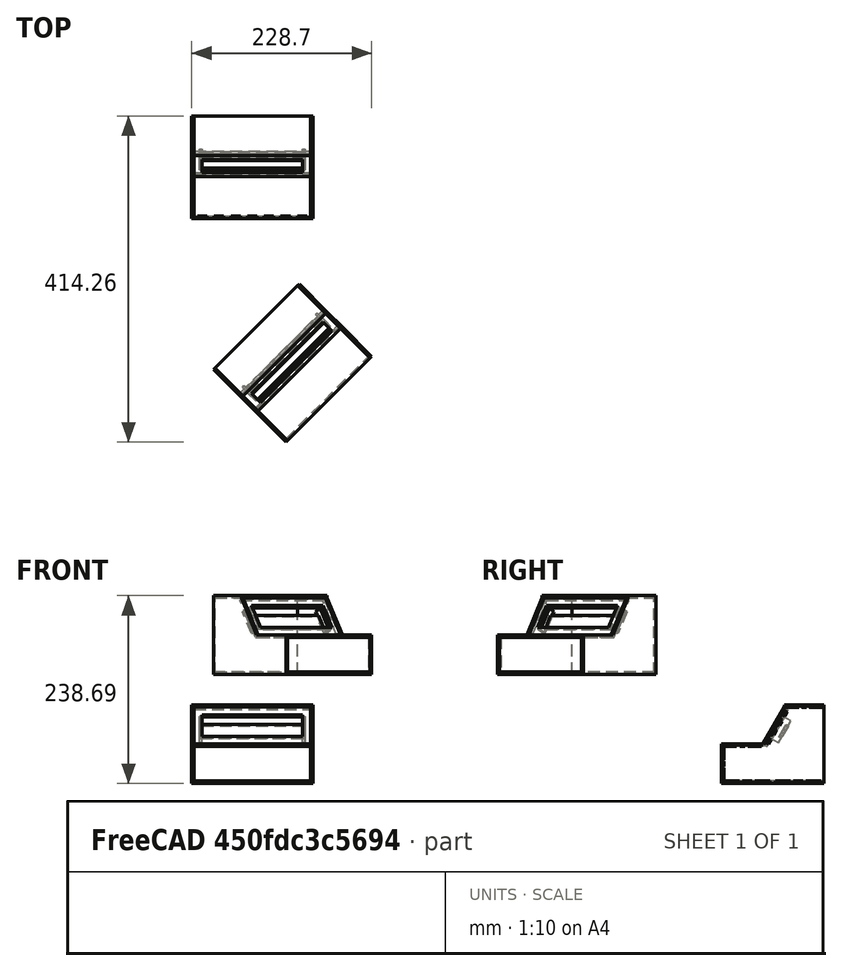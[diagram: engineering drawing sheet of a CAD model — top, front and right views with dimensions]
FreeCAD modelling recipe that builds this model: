
FCSTD DOCUMENT  (FreeCAD 0.21R33668 +26 (Git))
Label: support_4_matrix
License: All rights reserved
LicenseURL: https://en.wikipedia.org/wiki/All_rights_reserved
objects: Part::Feature×36, Sketcher::SketchObject×18, PartDesign::Pad×11, PartDesign::Body×11, Part::Part2DObjectPython×11, PartDesign::Pocket×7, App::DocumentObjectGroup×7, Part::FeaturePython×5, App::FeaturePython×4, Spreadsheet::Sheet×1, PartDesign::Plane×1, App::Part×1
note: 118 computed .brp shape members not serialized (recipe doc carries the construction recipe); baked Part::Feature solids carry a one-line shape summary decoded from their .brp

FEATURE [Sketcher::SketchObject] Sketch
  FullyConstrained = true
  MapMode = 5
  Placement = pos=(0,0,0) rot=(1,0,0;1.5708rad)
  Support = -> [XZ_Plane]
  expr: Constraints[10] = <<dimensions>>.lg_plaque
  expr: Constraints[9] = <<dimensions>>.ep_plaque
  sketch-geometry (4):
    g0: LineSegment StartX=0 StartY=0 StartZ=0 EndX=148 EndY=0 EndZ=0
    g1: LineSegment StartX=148 StartY=0 StartZ=0 EndX=148 EndY=3 EndZ=0
    g2: LineSegment StartX=148 StartY=3 StartZ=0 EndX=0 EndY=3 EndZ=0
    g3: LineSegment StartX=0 StartY=3 StartZ=0 EndX=0 EndY=0 EndZ=0
  constraints (11):
    c: Coincident(g0,g1)
    c: Coincident(g1,g2)
    c: Coincident(g2,g3)
    c: Coincident(g3,g0)
    c: Horizontal(g0)
    c: Horizontal(g2)
    c: Vertical(g1)
    c: Vertical(g3)
    c: Coincident(g0,g-1)
    c: DistanceY(g3,g3) = 3
    c: DistanceX(g2,g2) = 148
FEATURE [Spreadsheet::Sheet] Spreadsheet  label="dimensions"
  cells = A1='ep_plaque; B1='lrg_plaque; C1='lg_plaque; E1='ht_plaque; A2(ep_plaque)==3 mm; B2(lrg_plaque)==130 mm; C2(lg_plaque)==4 * lrg_matrix + 2 * dist_lateral_matrix; D2='4*32+2*2; E2(ht_plaque)==100 mm; F2='32+50+2; E3='ht_plat; A4='angle_display; B4='dist_top; E4(ht_plat)==50 mm; A5(angle_display)==120 °; B5(dist_top)==50 mm; E5='ht_display; E6==lg_display * cos(180 ° - (180 ° - angle_display) - 90 °); A7='lg_display; B7='dist_display; C7='lg_display = hypotenus; F7='Sin/cos -> degres by default; A8(lg_display)==(ht_plaque - ht_plat - ep_plaque) / sin(180 ° - angle_display); B8(dist_display)==(ht_plaque - ht_plat - ep_plaque) * cos(180 ° - angle_display) / sin(180 ° - angle_display); B10='dist_plat; B11(dist_plat)==lrg_plaque - dist_top - dist_display; A13='lrg_matrix; B13='dist_lateral_matrix; D13='ep_supp_ar; A14(lrg_matrix)==32 mm; B14(dist_lateral_matrix)==10 mm; D14(ep_supp_ar)==7 mm + ep_plaque; E14='Epaisseur; D15='ep_protu_supp_arr; D16(ep_protu_supp_ar)==10 mm; E16='Epaisseur protusion; A17='Informations; B17='Limitation /!\; D17='lg_side_supp; A18='Le trou de l'afficheur est centré; D18(lg_side_supp)==8 mm; D19='dph_supp; D20(dph_supp)==7 mm; D21='lrg_supp_ar; D22(lrg_supp_ar)==18 mm
FEATURE [PartDesign::Pad] Pad
  Direction = (0,-1,-2e-16)
  Length = 130
  Length2 = 10
  Placement = pos=(0,0,0) rot=(1,0,0;1.5708rad)
  Profile = -> Sketch
  ReferenceAxis = -> Sketch [N_Axis]
  Type = 0
  expr: Length = <<dimensions>>.lrg_plaque
FEATURE [PartDesign::Body] Body  label="plaque_dessous"
  Group = -> [Sketch,Pad]
  Origin = -> Origin
  Tip = -> Pad
FEATURE [Sketcher::SketchObject] Sketch001
  FullyConstrained = true
  MapMode = 5
  Support = -> [XY_Plane001]
  expr: Constraints[10] = <<dimensions>>.lrg_plaque
  expr: Constraints[9] = <<dimensions>>.ep_plaque
  sketch-geometry (4):
    g0: LineSegment StartX=-3 StartY=-130 StartZ=0 EndX=0 EndY=-130 EndZ=0
    g1: LineSegment StartX=0 StartY=-130 StartZ=0 EndX=0 EndY=0 EndZ=0
    g2: LineSegment StartX=0 StartY=0 StartZ=0 EndX=-3 EndY=0 EndZ=0
    g3: LineSegment StartX=-3 StartY=0 StartZ=0 EndX=-3 EndY=-130 EndZ=0
  constraints (11):
    c: Coincident(g0,g1)
    c: Coincident(g1,g2)
    c: Coincident(g2,g3)
    c: Coincident(g3,g0)
    c: Horizontal(g0)
    c: Horizontal(g2)
    c: Vertical(g1)
    c: Vertical(g3)
    c: Coincident(g1,g-1)
    c: DistanceX(g2,g2) = 3
    c: DistanceY(g3,g3) = 130
FEATURE [PartDesign::Pad] Pad001
  Direction = (0,0,1)
  Length = 100
  Length2 = 10
  Profile = -> Sketch001
  ReferenceAxis = -> Sketch001 [N_Axis]
  Type = 0
  expr: Length = <<dimensions>>.ht_plaque
FEATURE [Sketcher::SketchObject] Sketch002
  ExternalGeometry = -> [Pad001]
  FullyConstrained = true
  MapMode = 5
  Placement = pos=(-3,0,0) rot=(0.57735,-0.57735,-0.57735;2.0944rad)
  Support = -> [Pad001]
  expr: Constraints[11] = <<dimensions>>.angle_display
  expr: Constraints[12] = <<dimensions>>.dist_top
  expr: Constraints[13] = <<dimensions>>.ht_plaque - <<dimensions>>.ep_plaque
  expr: Constraints[6] = <<dimensions>>.ht_plat
  sketch-geometry (5):
    g0: LineSegment StartX=50 StartY=100 StartZ=0 EndX=130 EndY=100 EndZ=0
    g1: LineSegment StartX=130 StartY=100 StartZ=0 EndX=130 EndY=50 EndZ=0
    g2: LineSegment StartX=130 StartY=50 StartZ=0 EndX=77.1355 EndY=50 EndZ=0
    g3: LineSegment StartX=50 StartY=100 StartZ=0 EndX=50 EndY=97 EndZ=0
    g4: LineSegment StartX=50 StartY=97 StartZ=0 EndX=77.1355 EndY=50 EndZ=0
  constraints (14):
    c: Horizontal(g0)
    c: Coincident(g0,g1)
    c: Coincident(g1,g2)
    c: Horizontal(g2)
    c: Coincident(g0,g-4)
    c: PointOnObject(g1,g-4)
    c: DistanceY(g-4,g1) = 50
    c: Coincident(g0,g3)
    c: Vertical(g3)
    c: Coincident(g3,g4)
    c: Coincident(g4,g2)
    c: Angle(g2,g4) = 2.0944
    c: DistanceX(g-1,g3) = 50
    c: DistanceY(g-1,g3) = 97
FEATURE [PartDesign::Pocket] Pocket
  BaseFeature = -> Pad001
  Direction = (1,0,0)
  Length = 5
  Length2 = 5
  Profile = -> Sketch002
  ReferenceAxis = -> Sketch002 [N_Axis]
  Type = 1
FEATURE [PartDesign::Body] Body001  label="plaque_gauche"
  Group = -> [Sketch001,Pad001,Sketch002,Pocket]
  Origin = -> Origin001
  Tip = -> Pocket
FEATURE [Sketcher::SketchObject] Sketch003
  FullyConstrained = true
  MapMode = 5
  Support = -> [XY_Plane002]
  expr: Constraints[10] = <<dimensions>>.lg_plaque
  expr: Constraints[11] = <<dimensions>>.lrg_plaque
  expr: Constraints[9] = <<dimensions>>.ep_plaque
  sketch-geometry (4):
    g0: LineSegment StartX=148 StartY=0 StartZ=0 EndX=151 EndY=0 EndZ=0
    g1: LineSegment StartX=151 StartY=0 StartZ=0 EndX=151 EndY=-130 EndZ=0
    g2: LineSegment StartX=151 StartY=-130 StartZ=0 EndX=148 EndY=-130 EndZ=0
    g3: LineSegment StartX=148 StartY=-130 StartZ=0 EndX=148 EndY=0 EndZ=0
  constraints (12):
    c: Coincident(g0,g1)
    c: Coincident(g1,g2)
    c: Coincident(g2,g3)
    c: Coincident(g3,g0)
    c: Horizontal(g0)
    c: Horizontal(g2)
    c: Vertical(g1)
    c: Vertical(g3)
    c: PointOnObject(g0,g-1)
    c: DistanceX(g0,g0) = 3
    c: DistanceX(g-1,g0) = 148
    c: DistanceY(g1,g1) = 130
FEATURE [PartDesign::Pad] Pad002
  Direction = (0,0,1)
  Length = 100
  Length2 = 10
  Profile = -> Sketch003
  ReferenceAxis = -> Sketch003 [N_Axis]
  Type = 0
  expr: Length = <<dimensions>>.ht_plaque
FEATURE [Sketcher::SketchObject] Sketch004
  ExternalGeometry = -> [Pad002]
  FullyConstrained = true
  MapMode = 5
  Placement = pos=(151,0,0) rot=(0.57735,0.57735,0.57735;2.0944rad)
  Support = -> [Pad002]
  expr: Constraints[10] = <<dimensions>>.ht_plaque - <<dimensions>>.ep_plaque
  expr: Constraints[13] = <<dimensions>>.dist_top
  expr: Constraints[6] = <<dimensions>>.angle_display
  expr: Constraints[7] = <<dimensions>>.ht_plat
  sketch-geometry (5):
    g0: LineSegment StartX=-130 StartY=50 StartZ=0 EndX=-77.1355 EndY=50 EndZ=0
    g1: LineSegment StartX=-50 StartY=100 StartZ=0 EndX=-130 EndY=100 EndZ=0
    g2: LineSegment StartX=-130 StartY=100 StartZ=0 EndX=-130 EndY=50 EndZ=0
    g3: LineSegment StartX=-50 StartY=100 StartZ=0 EndX=-50 EndY=97 EndZ=0
    g4: LineSegment StartX=-50 StartY=97 StartZ=0 EndX=-77.1355 EndY=50 EndZ=0
  constraints (14):
    c: Coincident(g1,g2)
    c: Coincident(g2,g0)
    c: Coincident(g1,g-4)
    c: Coincident(g1,g3)
    c: Coincident(g3,g4)
    c: Coincident(g4,g0)
    c: Angle(g4,g0) = 2.0944
    c: DistanceY(g-4,g0) = 50
    c: Perpendicular(g0,g2)
    c: PointOnObject(g0,g-4)
    c: DistanceY(g-4,g3) = 97
    c: PointOnObject(g1,g-3)
    c: Perpendicular(g3,g1)
    c: DistanceX(g1,g-3) = 50
FEATURE [PartDesign::Pocket] Pocket001
  BaseFeature = -> Pad002
  Direction = (-1,0,0)
  Length = 5
  Length2 = 5
  Profile = -> Sketch004
  ReferenceAxis = -> Sketch004 [N_Axis]
  Type = 1
FEATURE [PartDesign::Body] Body002  label="plaque_droite"
  Group = -> [Sketch003,Pad002,Sketch004,Pocket001]
  Origin = -> Origin002
  Tip = -> Pocket001
FEATURE [Sketcher::SketchObject] Sketch005
  FullyConstrained = true
  MapMode = 5
  Placement = pos=(0,0,0) rot=(0.57735,0.57735,0.57735;2.0944rad)
  Support = -> [YZ_Plane003]
  expr: Constraints[10] = <<dimensions>>.ht_plaque
  expr: Constraints[11] = <<dimensions>>.ep_plaque
  expr: Constraints[9] = <<dimensions>>.dist_top
  sketch-geometry (4):
    g0: LineSegment StartX=-50 StartY=97 StartZ=0 EndX=0 EndY=97 EndZ=0
    g1: LineSegment StartX=0 StartY=97 StartZ=0 EndX=0 EndY=100 EndZ=0
    g2: LineSegment StartX=0 StartY=100 StartZ=0 EndX=-50 EndY=100 EndZ=0
    g3: LineSegment StartX=-50 StartY=100 StartZ=0 EndX=-50 EndY=97 EndZ=0
  constraints (12):
    c: Coincident(g0,g1)
    c: Coincident(g1,g2)
    c: Coincident(g2,g3)
    c: Coincident(g3,g0)
    c: Horizontal(g0)
    c: Horizontal(g2)
    c: Vertical(g1)
    c: Vertical(g3)
    c: PointOnObject(g0,g-2)
    c: DistanceX(g0,g0) = 50
    c: DistanceY(g-1,g1) = 100
    c: DistanceY(g1,g1) = 3
FEATURE [PartDesign::Pad] Pad003
  Direction = (1,-2e-16,3e-16)
  Length = 148
  Length2 = 10
  Placement = pos=(0,0,0) rot=(0.57735,0.57735,0.57735;2.0944rad)
  Profile = -> Sketch005
  ReferenceAxis = -> Sketch005 [N_Axis]
  Type = 0
  expr: Length = <<dimensions>>.lg_plaque
FEATURE [PartDesign::Body] Body003  label="plaque_dessus_haut"
  Group = -> [Sketch005,Pad003]
  Origin = -> Origin003
  Tip = -> Pad003
FEATURE [Sketcher::SketchObject] Sketch006
  FullyConstrained = true
  MapMode = 5
  Placement = pos=(0,0,0) rot=(0.57735,0.57735,0.57735;2.0944rad)
  Support = -> [YZ_Plane004]
  expr: Constraints[10] = <<dimensions>>.ht_plat - <<dimensions>>.ep_plaque * cos(180 ° - <<dimensions>>.angle_display)
  expr: Constraints[11] = <<dimensions>>.ht_plaque - <<dimensions>>.ep_plaque * sin(<<dimensions>>.angle_display - 90 °) - <<dimensions>>.ep_plaque
  expr: Constraints[4] = <<dimensions>>.ht_plat
  expr: Constraints[5] = <<dimensions>>.dist_top + <<dimensions>>.dist_display
  expr: Constraints[6] = <<dimensions>>.ht_plaque - <<dimensions>>.ep_plaque
  expr: Constraints[7] = <<dimensions>>.dist_top
  sketch-geometry (4):
    g0: LineSegment StartX=-74.5374 StartY=48.5 StartZ=0 EndX=-47.4019 EndY=95.5 EndZ=0
    g1: LineSegment StartX=-47.4019 StartY=95.5 StartZ=0 EndX=-50 EndY=97 EndZ=0
    g2: LineSegment StartX=-50 StartY=97 StartZ=0 EndX=-77.1355 EndY=50 EndZ=0
    g3: LineSegment StartX=-77.1355 StartY=50 StartZ=0 EndX=-74.5374 EndY=48.5 EndZ=0
  constraints (12):
    c: Coincident(g0,g1)
    c: Coincident(g1,g2)
    c: Coincident(g2,g3)
    c: Coincident(g3,g0)
    c: DistanceY(g-1,g2) = 50
    c: DistanceX(g2,g-1) = 77.1355
    c: DistanceY(g-1,g1) = 97
    c: DistanceX(g1,g-1) = 50
    c: Perpendicular(g3,g2)
    c: Perpendicular(g2,g1)
    c: DistanceY(g-1,g0) = 48.5
    c: DistanceY(g-1,g0) = 95.5
FEATURE [Sketcher::SketchObject] Sketch008
  FullyConstrained = true
  MapMode = 5
  Placement = pos=(0,0,0) rot=(0.57735,0.57735,0.57735;2.0944rad)
  Support = -> [YZ_Plane005]
  expr: Constraints[10] = <<dimensions>>.lrg_plaque
  expr: Constraints[11] = <<dimensions>>.ht_plat
  expr: Constraints[8] = <<dimensions>>.ep_plaque
  expr: Constraints[9] = <<dimensions>>.dist_plat
  sketch-geometry (4):
    g0: LineSegment StartX=-130 StartY=50 StartZ=0 EndX=-77.1355 EndY=50 EndZ=0
    g1: LineSegment StartX=-77.1355 StartY=50 StartZ=0 EndX=-77.1355 EndY=47 EndZ=0
    g2: LineSegment StartX=-77.1355 StartY=47 StartZ=0 EndX=-130 EndY=47 EndZ=0
    g3: LineSegment StartX=-130 StartY=47 StartZ=0 EndX=-130 EndY=50 EndZ=0
  constraints (12):
    c: Coincident(g0,g1)
    c: Coincident(g1,g2)
    c: Coincident(g2,g3)
    c: Coincident(g3,g0)
    c: Horizontal(g0)
    c: Horizontal(g2)
    c: Vertical(g1)
    c: Vertical(g3)
    c: DistanceY(g3,g3) = 3
    c: DistanceX(g0,g0) = 52.8645
    c: DistanceX(g0,g-1) = 130
    c: DistanceY(g-1,g0) = 50
FEATURE [PartDesign::Pad] Pad005
  Direction = (1,-2e-16,3e-16)
  Length = 148
  Length2 = 10
  Placement = pos=(0,0,0) rot=(0.57735,0.57735,0.57735;2.0944rad)
  Profile = -> Sketch008
  ReferenceAxis = -> Sketch008 [N_Axis]
  Type = 0
  expr: Length = <<dimensions>>.lg_plaque
FEATURE [PartDesign::Body] Body005  label="plaque_plat"
  Group = -> [Sketch008,Pad005]
  Origin = -> Origin005
  Tip = -> Pad005
FEATURE [Sketcher::SketchObject] Sketch009
  FullyConstrained = true
  MapMode = 5
  Placement = pos=(0,0,0) rot=(0.57735,0.57735,0.57735;2.0944rad)
  Support = -> [YZ_Plane006]
  expr: Constraints[10] = <<dimensions>>.lrg_plaque
  expr: Constraints[11] = <<dimensions>>.ht_plat - 2 * <<dimensions>>.ep_plaque
  expr: Constraints[8] = <<dimensions>>.ep_plaque
  expr: Constraints[9] = <<dimensions>>.ht_plat - <<dimensions>>.ep_plaque
  sketch-geometry (4):
    g0: LineSegment StartX=-130 StartY=47 StartZ=0 EndX=-127 EndY=47 EndZ=0
    g1: LineSegment StartX=-127 StartY=47 StartZ=0 EndX=-127 EndY=3 EndZ=0
    g2: LineSegment StartX=-127 StartY=3 StartZ=0 EndX=-130 EndY=3 EndZ=0
    g3: LineSegment StartX=-130 StartY=3 StartZ=0 EndX=-130 EndY=47 EndZ=0
  constraints (12):
    c: Coincident(g0,g1)
    c: Coincident(g1,g2)
    c: Coincident(g2,g3)
    c: Coincident(g3,g0)
    c: Horizontal(g0)
    c: Horizontal(g2)
    c: Vertical(g1)
    c: Vertical(g3)
    c: DistanceX(g0,g0) = 3
    c: DistanceY(g-1,g0) = 47
    c: DistanceX(g0,g-1) = 130
    c: DistanceY(g1,g1) = 44
FEATURE [PartDesign::Pad] Pad006
  Direction = (1,-2e-16,3e-16)
  Length = 148
  Length2 = 10
  Placement = pos=(0,0,0) rot=(0.57735,0.57735,0.57735;2.0944rad)
  Profile = -> Sketch009
  ReferenceAxis = -> Sketch009 [N_Axis]
  Type = 0
  expr: Length = <<dimensions>>.lg_plaque
FEATURE [PartDesign::Body] Body006  label="plaque_avant"
  Group = -> [Sketch009,Pad006]
  Origin = -> Origin006
  Tip = -> Pad006
FEATURE [PartDesign::Pad] Pad007
  Direction = (1,-2e-16,3e-16)
  Length = 148
  Length2 = 10
  Placement = pos=(0,0,0) rot=(0.57735,0.57735,0.57735;2.0944rad)
  Profile = -> Sketch006
  ReferenceAxis = -> Sketch006 [N_Axis]
  Type = 0
  expr: Length = <<dimensions>>.lg_plaque
FEATURE [Sketcher::SketchObject] Sketch010
  ExternalGeometry = -> [Pad007]
  FullyConstrained = true
  MapMode = 5
  Placement = pos=(-4.77e-14,-79.5022,45.9006) rot=(0.447214,0.447214,-0.774597;1.82348rad)
  Support = -> [Pad007]
  expr: Constraints[10] = (<<dimensions>>.lg_plaque - 4 * <<dimensions>>.lrg_matrix) / 2
  expr: Constraints[11] = (<<dimensions>>.lg_display - <<dimensions>>.lrg_matrix) / 2
  expr: Constraints[8] = <<dimensions>>.lrg_matrix
  expr: Constraints[9] = <<dimensions>>.lrg_matrix * 4
  sketch-geometry (4):
    g0: LineSegment StartX=-47.869 StartY=10 StartZ=0 EndX=-15.869 EndY=10 EndZ=0
    g1: LineSegment StartX=-15.869 StartY=10 StartZ=0 EndX=-15.869 EndY=138 EndZ=0
    g2: LineSegment StartX=-15.869 StartY=138 StartZ=0 EndX=-47.869 EndY=138 EndZ=0
    g3: LineSegment StartX=-47.869 StartY=138 StartZ=0 EndX=-47.869 EndY=10 EndZ=0
  constraints (12):
    c: Coincident(g0,g1)
    c: Coincident(g1,g2)
    c: Coincident(g2,g3)
    c: Coincident(g3,g0)
    c: Horizontal(g0)
    c: Horizontal(g2)
    c: Vertical(g1)
    c: Vertical(g3)
    c: DistanceX(g0,g0) = 32
    c: DistanceY(g3,g3) = 128
    c: DistanceY(g-1,g0) = 10
    c: DistanceX(g0,g-3) = 11.1355
FEATURE [PartDesign::Pocket] Pocket002
  BaseFeature = -> Pad007
  Direction = (6e-16,0.866025,-0.5)
  Length = 5
  Length2 = 5
  Placement = pos=(0,0,0) rot=(0.57735,0.57735,0.57735;2.0944rad)
  Profile = -> Sketch010
  ReferenceAxis = -> Sketch010 [N_Axis]
  Type = 1
FEATURE [PartDesign::Body] Body004  label="plaque_display"
  Group = -> [Sketch006,Pad007,Sketch010,Pocket002]
  Origin = -> Origin004
  Tip = -> Pocket002
FEATURE [Part::Feature] Body007  label="plaque_dessous001"
  shape: bbox 148 x 130 x 3 mm, 6 faces (baked)
FEATURE [Part::Feature] Body008  label="plaque_gauche001"
  shape: bbox 3 x 130 x 100 mm, 9 faces (baked)
FEATURE [Part::Feature] Body009  label="plaque_droite001"
  shape: bbox 3 x 130 x 100 mm, 9 faces (baked)
FEATURE [Part::Feature] Body010  label="plaque_dessus_haut001"
  shape: bbox 148 x 50 x 3 mm, 6 faces (baked)
FEATURE [Part::Feature] Body011  label="plaque_display001"
  shape: bbox 148 x 29.73 x 48.5 mm, 10 faces (baked)
FEATURE [Part::Feature] Body012  label="plaque_plat001"
  shape: bbox 148 x 52.86 x 3 mm, 6 faces (baked)
FEATURE [Part::Feature] Body013  label="plaque_avant001"
  shape: bbox 148 x 3 x 44 mm, 6 faces (baked)
FEATURE [App::DocumentObjectGroup] MultiJoin_origin_parts
  Group = -> [Body007,Body008,Body009,Body010,Body011,Body012,Body013]
FEATURE [Part::Feature] plaque_dessous001_tab
  shape: bbox 154 x 130 x 3 mm, 126 faces (baked)
FEATURE [Part::Feature] plaque_gauche001_tab
  shape: bbox 3 x 130 x 100 mm, 129 faces (baked)
FEATURE [Part::Feature] plaque_droite001_tab
  shape: bbox 3 x 130 x 100 mm, 129 faces (baked)
FEATURE [Part::Feature] plaque_dessus_haut001_tab
  shape: bbox 154 x 50 x 3 mm, 66 faces (baked)
FEATURE [Part::Feature] plaque_display001_tab
  shape: bbox 154 x 29.73 x 48.5 mm, 70 faces (baked)
FEATURE [Part::Feature] plaque_plat001_tab
  shape: bbox 154 x 52.86 x 3 mm, 66 faces (baked)
FEATURE [Part::Feature] plaque_avant001_tab
  shape: bbox 154 x 3 x 44 mm, 66 faces (baked)
FEATURE [Part::FeaturePython] MultiJoin  label="MultiJoin_V0"  # WARN: FeaturePython — macro-defined, semantics opaque (R4)
  fromParts = -> [MultiJoin_origin_parts,Body007,Body008,Body009,Body010,Body011,Body012,Body013]
  generatedParts = -> [plaque_dessous001_tab,plaque_gauche001_tab,plaque_droite001_tab,plaque_dessus_haut001_tab,plaque_display001_tab,plaque_plat001_tab,plaque_avant001_tab]
FEATURE [Part::FeaturePython] b_8x8_Dot_Matrix1_001_  label="8x8 Dot Matrix1_001"  # a2plus imported part (geometry in sourceFile) (typed FeaturePython)
  a2p_Version = 0.4.61
  fixedPosition = true
  objectType = a2pPart
  sourceFile = ./../../../../../../Téléchargements/8x8 Dot Matrix.step
  subassemblyImport = false
  timeLastImport = 1580202952
  updateColors = true
FEATURE [Sketcher::SketchObject] Sketch011
  FullyConstrained = true
  MapMode = 5
  Placement = pos=(0,0,0) rot=(0.57735,0.57735,0.57735;2.0944rad)
  Support = -> [YZ_Plane007]
  expr: Constraints[10] = <<dimensions>>.ht_plaque - 2 * <<dimensions>>.ep_plaque * sin(<<dimensions>>.angle_display - 90 °) - <<dimensions>>.ep_plaque
  expr: Constraints[11] = <<dimensions>>.dist_top - 2 * <<dimensions>>.ep_plaque * cos(<<dimensions>>.angle_display - 90 °)
  expr: Constraints[4] = <<dimensions>>.ht_plat - <<dimensions>>.ep_plaque * cos(180 ° - <<dimensions>>.angle_display)
  expr: Constraints[5] = <<dimensions>>.ht_plaque - <<dimensions>>.ep_plaque * sin(<<dimensions>>.angle_display - 90 °) - <<dimensions>>.ep_plaque
  expr: Constraints[6] = <<dimensions>>.lrg_plaque - <<dimensions>>.dist_plat - <<dimensions>>.ep_plaque * sin(180 ° - <<dimensions>>.angle_display)
  expr: Constraints[7] = <<dimensions>>.dist_top - <<dimensions>>.ep_plaque * cos(<<dimensions>>.angle_display - 90 °)
  expr: Constraints[8] = <<dimensions>>.lrg_plaque - <<dimensions>>.dist_plat - 2 * <<dimensions>>.ep_plaque * sin(180 ° - <<dimensions>>.angle_display)
  expr: Constraints[9] = <<dimensions>>.ht_plat - 2 * <<dimensions>>.ep_plaque * cos(180 ° - <<dimensions>>.angle_display)
  sketch-geometry (4):
    g0: LineSegment StartX=-74.5374 StartY=48.5 StartZ=0 EndX=-71.9393 EndY=47 EndZ=0
    g1: LineSegment StartX=-71.9393 StartY=47 StartZ=0 EndX=-44.8038 EndY=94 EndZ=0
    g2: LineSegment StartX=-44.8038 StartY=94 StartZ=0 EndX=-47.4019 EndY=95.5 EndZ=0
    g3: LineSegment StartX=-47.4019 StartY=95.5 StartZ=0 EndX=-74.5374 EndY=48.5 EndZ=0
  constraints (12):
    c: Coincident(g0,g1)
    c: Coincident(g1,g2)
    c: Coincident(g2,g3)
    c: Coincident(g3,g0)
    c: DistanceY(g-1,g0) = 48.5
    c: DistanceY(g-1,g2) = 95.5
    c: DistanceX(g0,g-1) = 74.5374
    c: DistanceX(g2,g-1) = 47.4019
    c: DistanceX(g0,g-1) = 71.9393
    c: DistanceY(g-1,g0) = 47
    c: DistanceY(g-1,g1) = 94
    c: DistanceX(g1,g-1) = 44.8038
FEATURE [PartDesign::Pad] Pad008
  Direction = (1,-2e-16,3e-16)
  Length = 148
  Length2 = 10
  Placement = pos=(0,0,0) rot=(0.57735,0.57735,0.57735;2.0944rad)
  Profile = -> Sketch011
  ReferenceAxis = -> Sketch011 [N_Axis]
  Type = 0
  expr: Length = <<dimensions>>.lg_plaque
FEATURE [Sketcher::SketchObject] Sketch012
  ExternalGeometry = -> [Pad008]
  FullyConstrained = true
  MapMode = 5
  Placement = pos=(-4.62e-14,-76.9042,44.4006) rot=(0.447214,0.447214,-0.774597;1.82348rad)
  Support = -> [Pad008]
  expr: Constraints[10] = (<<dimensions>>.lg_plaque - 4 * <<dimensions>>.lrg_matrix) / 2
  expr: Constraints[11] = (<<dimensions>>.lg_display - <<dimensions>>.lrg_matrix) / 2
  expr: Constraints[8] = <<dimensions>>.lrg_matrix
  expr: Constraints[9] = 4 * <<dimensions>>.lrg_matrix
  sketch-geometry (4):
    g0: LineSegment StartX=-47.869 StartY=138 StartZ=0 EndX=-15.869 EndY=138 EndZ=0
    g1: LineSegment StartX=-15.869 StartY=138 StartZ=0 EndX=-15.869 EndY=10 EndZ=0
    g2: LineSegment StartX=-15.869 StartY=10 StartZ=0 EndX=-47.869 EndY=10 EndZ=0
    g3: LineSegment StartX=-47.869 StartY=10 StartZ=0 EndX=-47.869 EndY=138 EndZ=0
  constraints (12):
    c: Coincident(g0,g1)
    c: Coincident(g1,g2)
    c: Coincident(g2,g3)
    c: Coincident(g3,g0)
    c: Horizontal(g0)
    c: Horizontal(g2)
    c: Vertical(g1)
    c: Vertical(g3)
    c: DistanceX(g2,g2) = 32
    c: DistanceY(g1,g1) = 128
    c: DistanceY(g-1,g1) = 10
    c: DistanceX(g1,g-4) = 11.1355
FEATURE [PartDesign::Pocket] Pocket003
  BaseFeature = -> Pad008
  Direction = (6e-16,0.866025,-0.5)
  Length = 5
  Length2 = 5
  Placement = pos=(0,0,0) rot=(0.57735,0.57735,0.57735;2.0944rad)
  Profile = -> Sketch012
  ReferenceAxis = -> Sketch012 [N_Axis]
  Type = 1
  expr: Length = 5 mm
FEATURE [PartDesign::Body] Body014  label="plaque_display_2"
  Group = -> [Sketch011,Pad008,Sketch012,Pocket003]
  Origin = -> Origin007
  Tip = -> Pocket003
FEATURE [Sketcher::SketchObject] Sketch013
  FullyConstrained = true
  MapMode = 5
  Placement = pos=(0,0,0) rot=(0.57735,0.57735,0.57735;2.0944rad)
  Support = -> [YZ_Plane008]
  expr: Constraints[11] = <<dimensions>>.lg_display
  expr: Constraints[4] = <<dimensions>>.dist_top - 2 * <<dimensions>>.ep_plaque * cos(<<dimensions>>.angle_display - 90 °)
  expr: Constraints[5] = <<dimensions>>.ht_plaque - <<dimensions>>.ep_plaque - 2 * <<dimensions>>.ep_plaque * sin(<<dimensions>>.angle_display - 90 °)
  expr: Constraints[6] = <<dimensions>>.dist_top - (2 * <<dimensions>>.ep_plaque + <<dimensions>>.ep_supp_ar) * cos(<<dimensions>>.angle_display - 90 °)
  expr: Constraints[7] = <<dimensions>>.ht_plaque - <<dimensions>>.ep_plaque - (2 * <<dimensions>>.ep_plaque + <<dimensions>>.ep_supp_ar) * sin(<<dimensions>>.angle_display - 90 °)
  sketch-geometry (4):
    g0: LineSegment StartX=-71.9393 StartY=47 StartZ=0 EndX=-63.2791 EndY=42 EndZ=0
    g1: LineSegment StartX=-63.2791 StartY=42 StartZ=0 EndX=-36.1436 EndY=89 EndZ=0
    g2: LineSegment StartX=-36.1436 StartY=89 StartZ=0 EndX=-44.8038 EndY=94 EndZ=0
    g3: LineSegment StartX=-44.8038 StartY=94 StartZ=0 EndX=-71.9393 EndY=47 EndZ=0
  constraints (12):
    c: Coincident(g0,g1)
    c: Coincident(g1,g2)
    c: Coincident(g2,g3)
    c: Coincident(g3,g0)
    c: DistanceX(g2,g-1) = 44.8038
    c: DistanceY(g-1,g2) = 94
    c: DistanceX(g1,g-1) = 36.1436
    c: DistanceY(g-1,g1) = 89
    c: Perpendicular(g2,g3)
    c: Perpendicular(g1,g2)
    c: Perpendicular(g1,g0)
    c: Distance(g2,g0) = 54.2709
FEATURE [PartDesign::Pad] Pad009
  Direction = (1,-2e-16,3e-16)
  Length = 10
  Length2 = 10
  Placement = pos=(0,0,0) rot=(0.57735,0.57735,0.57735;2.0944rad)
  Profile = -> Sketch013
  ReferenceAxis = -> Sketch013 [N_Axis]
  Type = 0
  expr: Length = (<<dimensions>>.lg_plaque - 4 * <<dimensions>>.lrg_matrix) / 2
FEATURE [Sketcher::SketchObject] Sketch014
  ExternalGeometry = -> [Pad009]
  FullyConstrained = false
  MapMode = 5
  Placement = pos=(-3.94e-14,-65.6458,37.9006) rot=(0.654654,0.654654,0.377964;3.86433rad)
  Support = -> [Pad009]
  expr: Constraints[14] = (<<dimensions>>.lg_display - <<dimensions>>.lrg_matrix) / 2
  expr: Constraints[16] = (<<dimensions>>.lg_display - <<dimensions>>.lrg_matrix) / 2
  expr: Constraints[18] = <<dimensions>>.ep_plaque
  sketch-geometry (8):
    g0: LineSegment StartX=4.73354 StartY=10 StartZ=0 EndX=15.869 EndY=10 EndZ=0
    g1: LineSegment StartX=15.869 StartY=10 StartZ=0 EndX=15.869 EndY=7 EndZ=0
    g2: LineSegment StartX=15.869 StartY=7 StartZ=0 EndX=47.869 EndY=7 EndZ=0
    g3: LineSegment StartX=47.869 StartY=7 StartZ=0 EndX=47.869 EndY=10 EndZ=0
    g4: LineSegment StartX=47.869 StartY=10 StartZ=0 EndX=59.0045 EndY=10 EndZ=0
    g5: LineSegment StartX=59.0045 StartY=10 StartZ=0 EndX=59.0045 EndY=0 EndZ=0
    g6: LineSegment StartX=59.0045 StartY=0 StartZ=0 EndX=4.73354 EndY=0 EndZ=0
    g7: LineSegment StartX=4.73354 StartY=0 StartZ=0 EndX=4.73354 EndY=10 EndZ=0
  constraints (19):
    c: Horizontal(g0)
    c: Coincident(g0,g1)
    c: Coincident(g1,g2)
    c: Horizontal(g2)
    c: Coincident(g2,g3)
    c: Coincident(g3,g4)
    c: Horizontal(g4)
    c: Coincident(g4,g5)
    c: Coincident(g5,g6)
    c: Coincident(g6,g-3)
    c: Coincident(g6,g7)
    c: Coincident(g7,g0)
    c: Perpendicular(g2,g1)
    c: Perpendicular(g2,g3)
    c: DistanceX(g0,g0) = 11.1355
    c: Coincident(g0,g-4)
    c: DistanceX(g4,g4) = 11.1355
    c: Coincident(g4,g-4)
    c: DistanceY(g3,g3) = 3
FEATURE [PartDesign::Pocket] Pocket004
  BaseFeature = -> Pad009
  Direction = (-6e-16,-0.866025,0.5)
  Length = 5
  Length2 = 5
  Placement = pos=(0,0,0) rot=(0.57735,0.57735,0.57735;2.0944rad)
  Profile = -> Sketch014
  ReferenceAxis = -> Sketch014 [N_Axis]
  Type = 1
FEATURE [PartDesign::Body] Body015  label="support_gauche"
  Group = -> [Sketch013,Pad009,Sketch014,Pocket004]
  Origin = -> Origin008
  Tip = -> Pocket004
FEATURE [Sketcher::SketchObject] Sketch015
  FullyConstrained = true
  MapMode = 5
  Placement = pos=(0,0,0) rot=(0.57735,0.57735,0.57735;2.0944rad)
  Support = -> [YZ_Plane009]
  expr: Constraints[11] = <<dimensions>>.lg_display
  expr: Constraints[4] = <<dimensions>>.dist_top - 2 * <<dimensions>>.ep_plaque * cos(<<dimensions>>.angle_display - 90 °)
  expr: Constraints[5] = <<dimensions>>.ht_plaque - <<dimensions>>.ep_plaque - 2 * <<dimensions>>.ep_plaque * sin(<<dimensions>>.angle_display - 90 °)
  expr: Constraints[6] = <<dimensions>>.dist_top - (2 * <<dimensions>>.ep_plaque + <<dimensions>>.ep_supp_ar) * cos(<<dimensions>>.angle_display - 90 °)
  expr: Constraints[7] = <<dimensions>>.ht_plaque - <<dimensions>>.ep_plaque - (2 * <<dimensions>>.ep_plaque + <<dimensions>>.ep_supp_ar) * sin(<<dimensions>>.angle_display - 90 °)
  sketch-geometry (4):
    g0: LineSegment StartX=-71.9393 StartY=47 StartZ=0 EndX=-63.2791 EndY=42 EndZ=0
    g1: LineSegment StartX=-63.2791 StartY=42 StartZ=0 EndX=-36.1436 EndY=89 EndZ=0
    g2: LineSegment StartX=-36.1436 StartY=89 StartZ=0 EndX=-44.8038 EndY=94 EndZ=0
    g3: LineSegment StartX=-44.8038 StartY=94 StartZ=0 EndX=-71.9393 EndY=47 EndZ=0
  constraints (12):
    c: Coincident(g0,g1)
    c: Coincident(g1,g2)
    c: Coincident(g2,g3)
    c: Coincident(g3,g0)
    c: DistanceX(g2,g-1) = 44.8038
    c: DistanceY(g-1,g2) = 94
    c: DistanceX(g1,g-1) = 36.1436
    c: DistanceY(g-1,g1) = 89
    c: Perpendicular(g2,g3)
    c: Perpendicular(g1,g2)
    c: Perpendicular(g1,g0)
    c: Distance(g2,g0) = 54.2709
FEATURE [PartDesign::Pad] Pad010
  Direction = (1,-2e-16,3e-16)
  Length = 148
  Length2 = 10
  Placement = pos=(0,0,0) rot=(0.57735,0.57735,0.57735;2.0944rad)
  Profile = -> Sketch015
  ReferenceAxis = -> Sketch015 [N_Axis]
  Type = 0
  expr: Length = <<dimensions>>.lg_plaque
FEATURE [Sketcher::SketchObject] Sketch016
  FullyConstrained = false
  MapMode = 5
  Placement = pos=(-3.94e-14,-65.6458,37.9006) rot=(0.654654,0.654654,0.377964;3.86433rad)
  Support = -> [Pad010]
  expr: Constraints[8] = <<dimensions>>.lg_plaque - (<<dimensions>>.lg_plaque - 4 * <<dimensions>>.lrg_matrix) / 2
  sketch-geometry (4):
    g0: LineSegment StartX=1.9641 StartY=138 StartZ=0 EndX=68.5337 EndY=138 EndZ=0
    g1: LineSegment StartX=68.5337 StartY=138 StartZ=0 EndX=68.5337 EndY=0 EndZ=0
    g2: LineSegment StartX=68.5337 StartY=0 StartZ=0 EndX=1.9641 EndY=0 EndZ=0
    g3: LineSegment StartX=1.9641 StartY=0 StartZ=0 EndX=1.9641 EndY=138 EndZ=0
  constraints (10):
    c: Coincident(g0,g1)
    c: Coincident(g1,g2)
    c: Coincident(g2,g3)
    c: Coincident(g3,g0)
    c: Horizontal(g0)
    c: Horizontal(g2)
    c: Vertical(g1)
    c: Vertical(g3)
    c: DistanceY(g3,g3) = 138
    c: PointOnObject(g2,g-1)
FEATURE [PartDesign::Pocket] Pocket005
  BaseFeature = -> Pad010
  Direction = (-6e-16,-0.866025,0.5)
  Length = 5
  Length2 = 5
  Placement = pos=(0,0,0) rot=(0.57735,0.57735,0.57735;2.0944rad)
  Profile = -> Sketch016
  ReferenceAxis = -> Sketch016 [N_Axis]
  Type = 1
FEATURE [Sketcher::SketchObject] Sketch017
  ExternalGeometry = -> [Pocket005]
  FullyConstrained = true
  MapMode = 5
  Placement = pos=(-3.94e-14,-65.6458,37.9006) rot=(0.654654,0.654654,0.377964;3.86433rad)
  Support = -> [Pocket005]
  expr: Constraints[16] = (<<dimensions>>.lg_display - <<dimensions>>.lrg_matrix) / 2
  expr: Constraints[17] = (<<dimensions>>.lg_display - <<dimensions>>.lrg_matrix) / 2
  expr: Constraints[18] = <<dimensions>>.lrg_matrix
  expr: Constraints[19] = <<dimensions>>.ep_plaque
  expr: Constraints[20] = <<dimensions>>.ep_plaque
  expr: Constraints[22] = (<<dimensions>>.lg_plaque - 4 * <<dimensions>>.lrg_matrix) / 2
  sketch-geometry (8):
    g0: LineSegment StartX=4.73354 StartY=138 StartZ=0 EndX=4.73354 EndY=148 EndZ=0
    g1: LineSegment StartX=4.73354 StartY=148 StartZ=0 EndX=59.0045 EndY=148 EndZ=0
    g2: LineSegment StartX=59.0045 StartY=148 StartZ=0 EndX=59.0045 EndY=138 EndZ=0
    g3: LineSegment StartX=59.0045 StartY=138 StartZ=0 EndX=47.869 EndY=138 EndZ=0
    g4: LineSegment StartX=47.869 StartY=138 StartZ=0 EndX=47.869 EndY=141 EndZ=0
    g5: LineSegment StartX=47.869 StartY=141 StartZ=0 EndX=15.869 EndY=141 EndZ=0
    g6: LineSegment StartX=15.869 StartY=141 StartZ=0 EndX=15.869 EndY=138 EndZ=0
    g7: LineSegment StartX=15.869 StartY=138 StartZ=0 EndX=4.73354 EndY=138 EndZ=0
  constraints (23):
    c: Vertical(g0)
    c: Coincident(g0,g1)
    c: Horizontal(g1)
    c: Coincident(g1,g2)
    c: Coincident(g2,g3)
    c: Horizontal(g3)
    c: Coincident(g3,g4)
    c: Coincident(g4,g5)
    c: Horizontal(g5)
    c: Coincident(g5,g6)
    c: Coincident(g6,g7)
    c: Coincident(g7,g0)
    c: Horizontal(g7)
    c: Perpendicular(g5,g6)
    c: Perpendicular(g5,g4)
    c: Perpendicular(g1,g2)
    c: Distance(g0,g6) = 11.1355
    c: Distance(g3,g2) = 11.1355
    c: Distance(g5,g4) = 32
    c: Distance(g6,g5) = 3
    c: Distance(g4,g3) = 3
    c: Coincident(g0,g-3)
    c: Distance(g0,g0) = 10
FEATURE [PartDesign::Pocket] Pocket006
  BaseFeature = -> Pocket005
  Direction = (-7e-16,-0.866025,0.5)
  Length = 5
  Length2 = 5
  Placement = pos=(0,0,0) rot=(0.57735,0.57735,0.57735;2.0944rad)
  Profile = -> Sketch017
  ReferenceAxis = -> Sketch017 [N_Axis]
  Type = 1
FEATURE [PartDesign::Body] Body016  label="support_droite"
  Group = -> [Sketch015,Pad010,Sketch016,Pocket005,Sketch017,Pocket006]
  Origin = -> Origin009
  Tip = -> Pocket006
FEATURE [PartDesign::Plane] DatumPlane
  Length = 145.545
  MapMode = 45
  Placement = pos=(10,-54.0415,68) rot=(0.447214,0.774597,0.447214;1.82348rad)
  ResizeMode = 0
  Support = -> [Pocket004]
  Width = 152.128
FEATURE [Sketcher::SketchObject] Sketch018
  FullyConstrained = true
  MapMode = 5
  Placement = pos=(10,-54.0415,68) rot=(0.447214,0.774597,0.447214;1.82348rad)
  Support = -> [DatumPlane]
  expr: Constraints[10] = <<dimensions>>.ep_plaque
  expr: Constraints[11] = <<dimensions>>.ep_protu_supp_ar / 2
  expr: Constraints[8] = <<dimensions>>.lrg_supp_ar / 2
  expr: Constraints[9] = <<dimensions>>.lrg_supp_ar / 2
  sketch-geometry (4):
    g0: LineSegment StartX=2 StartY=9 StartZ=0 EndX=5 EndY=9 EndZ=0
    g1: LineSegment StartX=5 StartY=9 StartZ=0 EndX=5 EndY=-9 EndZ=0
    g2: LineSegment StartX=5 StartY=-9 StartZ=0 EndX=2 EndY=-9 EndZ=0
    g3: LineSegment StartX=2 StartY=-9 StartZ=0 EndX=2 EndY=9 EndZ=0
  constraints (12):
    c: Coincident(g0,g1)
    c: Coincident(g1,g2)
    c: Coincident(g2,g3)
    c: Coincident(g3,g0)
    c: Horizontal(g0)
    c: Horizontal(g2)
    c: Vertical(g1)
    c: Vertical(g3)
    c: DistanceY(g-1,g0) = 9
    c: DistanceY(g2,g-1) = 9
    c: DistanceX(g2,g1) = 3
    c: DistanceX(g-1,g0) = 5
FEATURE [PartDesign::Pad] Pad011
  Direction = (1,-4.4e-15,3.5e-15)
  Length = 128
  Length2 = 10
  Placement = pos=(10,-54.0415,68) rot=(0.447214,0.774597,0.447214;1.82348rad)
  Profile = -> Sketch018
  ReferenceAxis = -> Sketch018 [N_Axis]
  Type = 0
  expr: Length = 4 * <<dimensions>>.lrg_matrix
FEATURE [PartDesign::Body] Body017  label="support_ar"
  Group = -> [DatumPlane,Sketch018,Pad011]
  Origin = -> Origin010
  Tip = -> Pad011
FEATURE [App::DocumentObjectGroup] Group001  label="Multijoin_V0"
  Group = -> [MultiJoin]
FEATURE [Part::FeaturePython] b_8x8_Dot_Matrix1_001_001  label="8x8 Dot Matrix1_002"  # a2plus imported part (geometry in sourceFile) (typed FeaturePython)
  Placement = pos=(96.1924,-276.993,169.512) rot=(0,0,-1;0.785079rad)
  a2p_Version = 0.4.61
  fixedPosition = false
  objectType = a2pPart
  sourceFile = ./../../../../../../Téléchargements/8x8 Dot Matrix.step
  subassemblyImport = false
  timeLastImport = 1580202952
  updateColors = true
FEATURE [App::Part] Part  label="Part_support_led_matrix"
  Group = -> [Body001,Body003,Body004,Body005,Body006,Body014,Body015,Body016,Body017,Body,Body002]
  Origin = -> Origin011
FEATURE [App::DocumentObjectGroup] Group  label="Support_led_matrix"
  Group = -> [Spreadsheet,Part]
FEATURE [Part::FeaturePython] b_support_led_matrix1_001_  label="support_led_matrix1_001"  # a2plus imported part (geometry in sourceFile) (typed FeaturePython)
  Placement = pos=(26.9952,-320.187,138.693) rot=(0,0,1;0.785079rad)
  a2p_Version = 0.4.61
  fixedPosition = false
  objectType = a2pPart
  sourceFile = ./support_led_matrix.step
  subassemblyImport = false
  timeLastImport = 1.70186e+09
  updateColors = true
FEATURE [App::DocumentObjectGroup] Group003  label="Assemblage"
  Group = -> [b_8x8_Dot_Matrix1_001_001,b_support_led_matrix1_001_]
FEATURE [App::FeaturePython] planesParallel_001  label="planesParallel_001__support_led_matrix1_001"  # a2plus constraint (typed FeaturePython)
  Object1 = b_8x8_Dot_Matrix1_001_001
  Object2 = b_support_led_matrix1_001_
  ParentTreeObject = -> b_8x8_Dot_Matrix1_001_001
  SubElement1 = Face497
  SubElement2 = Face61
  Suppressed = false
  Type = planesParallel
  directionConstraint = 1
FEATURE [App::FeaturePython] planesParallel_001_mirror  label="planesParallel_001__8x8 Dot Matrix1_002"  # a2plus constraint (typed FeaturePython)
  Object1 = b_8x8_Dot_Matrix1_001_001
  Object2 = b_support_led_matrix1_001_
  ParentTreeObject = -> b_support_led_matrix1_001_
  SubElement1 = Face497
  SubElement2 = Face61
  Suppressed = false
  Type = planesParallel
  directionConstraint = 1
FEATURE [App::FeaturePython] planeCoincident_001  label="planeCoincident_001__support_led_matrix1_001"  # a2plus constraint (typed FeaturePython)
  Object1 = b_8x8_Dot_Matrix1_001_001
  Object2 = b_support_led_matrix1_001_
  ParentTreeObject = -> b_8x8_Dot_Matrix1_001_001
  SubElement1 = Face496
  SubElement2 = Face61
  Suppressed = false
  Type = plane
  directionConstraint = 0
  offset = 0
FEATURE [App::FeaturePython] planeCoincident_001_mirror  label="planeCoincident_001__8x8 Dot Matrix1_002"  # a2plus constraint (typed FeaturePython)
  Object1 = b_8x8_Dot_Matrix1_001_001
  Object2 = b_support_led_matrix1_001_
  ParentTreeObject = -> b_support_led_matrix1_001_
  SubElement1 = Face496
  SubElement2 = Face61
  Suppressed = false
  Type = plane
  directionConstraint = 0
  offset = 0
FEATURE [Part::Feature] Body018  label="plaque_gauche002"
  shape: bbox 3 x 130 x 100 mm, 9 faces (baked)
FEATURE [Part::Feature] Body019  label="plaque_dessus_haut002"
  shape: bbox 148 x 50 x 3 mm, 6 faces (baked)
FEATURE [Part::Feature] Body020  label="plaque_display002"
  shape: bbox 148 x 29.73 x 48.5 mm, 10 faces (baked)
FEATURE [Part::Feature] Body021  label="plaque_plat002"
  shape: bbox 148 x 52.86 x 3 mm, 6 faces (baked)
FEATURE [Part::Feature] Body022  label="plaque_avant002"
  shape: bbox 148 x 3 x 44 mm, 6 faces (baked)
FEATURE [Part::Feature] Body023  label="plaque_display_003"
  shape: bbox 148 x 29.73 x 48.5 mm, 10 faces (baked)
FEATURE [Part::Feature] Body024  label="support_gauche001"
  shape: bbox 3 x 24.66 x 32.71 mm, 6 faces (baked)
FEATURE [Part::Feature] Body025  label="support_droite001"
  shape: bbox 3 x 24.66 x 32.71 mm, 6 faces (baked)
FEATURE [Part::Feature] Body026  label="support_ar001"
  shape: bbox 128 x 11.6 x 17.09 mm, 6 faces (baked)
FEATURE [Part::Feature] Body027  label="plaque_dessous002"
  shape: bbox 148 x 130 x 3 mm, 6 faces (baked)
FEATURE [Part::Feature] Body028  label="plaque_droite002"
  shape: bbox 3 x 130 x 100 mm, 9 faces (baked)
FEATURE [App::DocumentObjectGroup] MultiJoin001_origin_parts
  Group = -> [Body018,Body019,Body020,Body021,Body022,Body023,Body024,Body025,Body026,Body027,Body028]
FEATURE [Part::Feature] plaque_gauche002_tab
  shape: bbox 3 x 130 x 100 mm, 89 faces (baked)
FEATURE [Part::Feature] plaque_dessus_haut002_tab
  shape: bbox 154 x 50 x 3 mm, 30 faces (baked)
FEATURE [Part::Feature] plaque_display002_tab
  shape: bbox 154 x 29.73 x 48.5 mm, 58 faces (baked)
FEATURE [Part::Feature] plaque_plat002_tab
  shape: bbox 154 x 52.86 x 3 mm, 58 faces (baked)
FEATURE [Part::Feature] plaque_avant002_tab
  shape: bbox 154 x 3 x 50 mm, 114 faces (baked)
FEATURE [Part::Feature] plaque_display_003_tab
  shape: bbox 154 x 29.73 x 48.5 mm, 90 faces (baked)
FEATURE [Part::Feature] support_gauche001_tab
  shape: bbox 3 x 26.81 x 33.43 mm, 38 faces (baked)
FEATURE [Part::Feature] support_droite001_tab
  shape: bbox 3 x 26.81 x 33.43 mm, 38 faces (baked)
FEATURE [Part::Feature] support_ar001_tab
  shape: bbox 134 x 11.6 x 17.09 mm, 30 faces (baked)
FEATURE [Part::Feature] plaque_dessous002_tab
  shape: bbox 154 x 130 x 3 mm, 106 faces (baked)
FEATURE [Part::Feature] plaque_droite002_tab
  shape: bbox 3 x 130 x 100 mm, 89 faces (baked)
FEATURE [Part::FeaturePython] MultiJoin001  # WARN: FeaturePython — macro-defined, semantics opaque (R4)
  fromParts = -> [MultiJoin001_origin_parts,Body018,Body019,Body020,Body021,Body022,Body023,Body024,Body025,Body026,Body027,Body028]
  generatedParts = -> [plaque_gauche002_tab,plaque_dessus_haut002_tab,plaque_display002_tab,plaque_plat002_tab,plaque_avant002_tab,plaque_display_003_tab,support_gauche001_tab,support_droite001_tab,support_ar001_tab,plaque_dessous002_tab,plaque_droite002_tab]
FEATURE [Part::Part2DObjectPython] Shape2DView  # Draft 2D object (typed FeaturePython)
  AutoUpdate = true
  Clip = false
  FuseArch = false
  HiddenLines = false
  InPlace = true
  OnlySolids = false
  Projection = (0,0,1)
  ProjectionMode = 0
  SegmentLength = 0.05
  Tessellation = false
  VisibleOnly = false
FEATURE [Part::Part2DObjectPython] Shape2DView001 .. Shape2DView010  x10 (patterned run collapsed; names and placements below)
  AutoUpdate = true
  Clip = false
  FuseArch = false
  HiddenLines = false
  InPlace = true
  OnlySolids = false
  Projection = (0,0,1)
  ProjectionMode = 0
  SegmentLength = 0.05
  Tessellation = false
  VisibleOnly = false
FEATURE [App::DocumentObjectGroup] Group004  label="Export"
  Group = -> [Shape2DView,Shape2DView001,Shape2DView002,Shape2DView003,Shape2DView004,Shape2DView005,Shape2DView006,Shape2DView007,Shape2DView008,Shape2DView009,Shape2DView010]
FEATURE [App::DocumentObjectGroup] Group002  label="Multijoin_V1"
  Group = -> [MultiJoin001,Group004]
